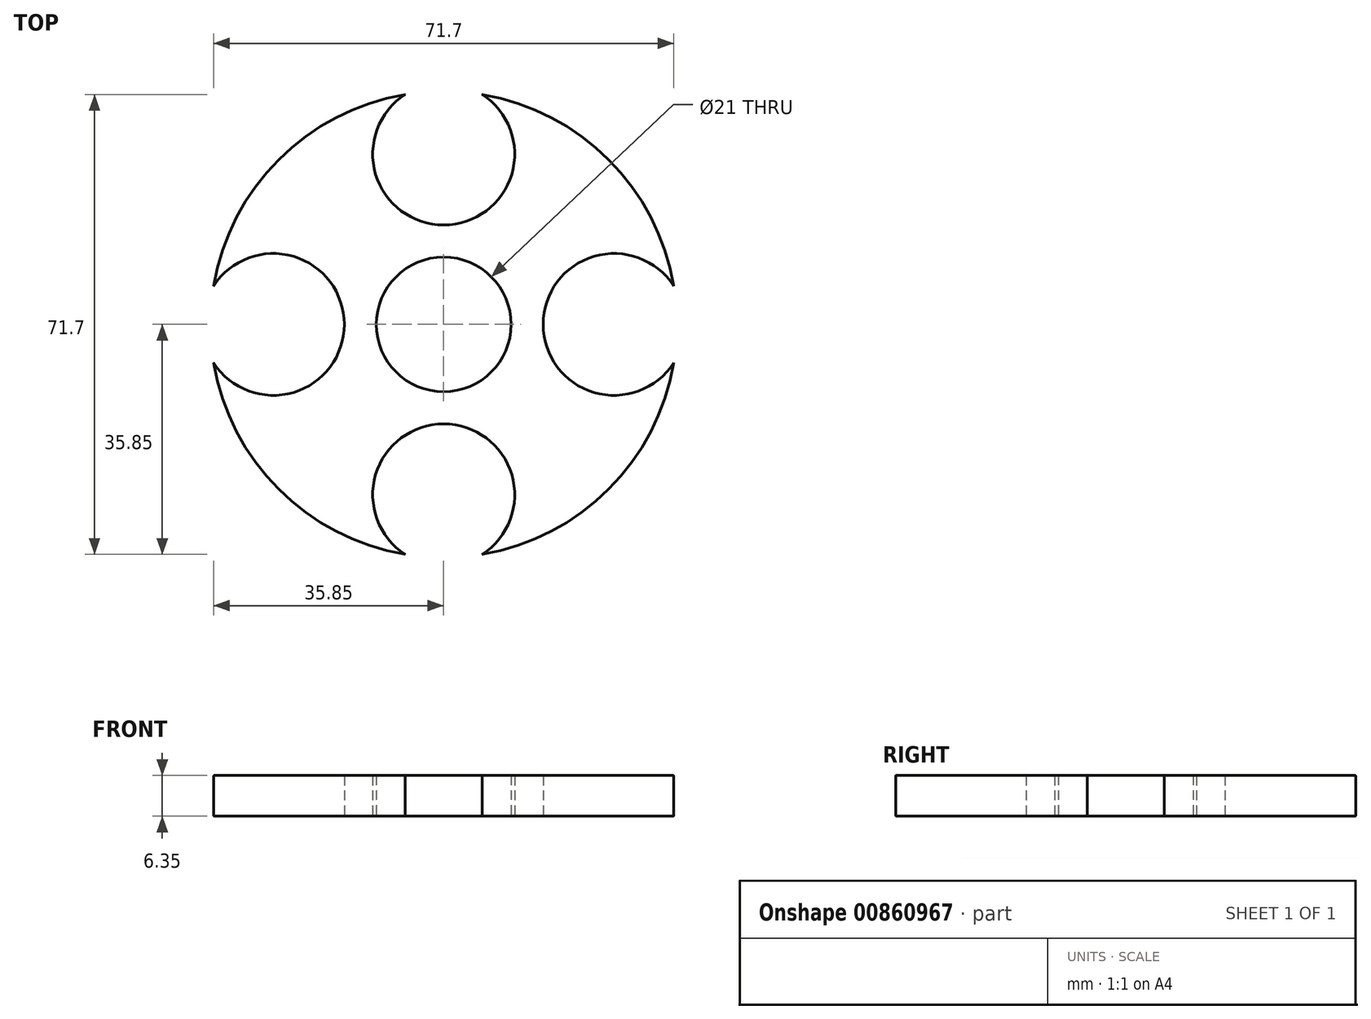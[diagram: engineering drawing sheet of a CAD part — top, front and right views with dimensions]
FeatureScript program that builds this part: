
annotation { "Feature Type Name" : "Feature", "Feature Type Description" : "" }
export const myFeature = defineFeature(function(context is Context, id is Id, definition is map)
    precondition{}
    {
        {
            var Q0;
            Q0=qCreatedBy(makeId("Top.planeOp"),FACE);
            var sketch = newSketch(context, id + "F0", { "sketchPlane" : qUnion([Q0])});
            skCircle(sketch, "E0", {"center": v(0, 0) * mm, "radius": 10.5 * mm});
            skArc(sketch, "E1", {"start": v(-35.85, -6) * mm, "mid": v(-25.7, -25.7) * mm, "end": v(-6.01, -35.85) * mm});
            skLineSegment(sketch, "E2", {"start": v(0, 10.5) * mm, "end": v(0, -11.46) * mm, "construction": true});
            skPoint(sketch, "E3.endSnap0", {"position": v(0, -0.48) * mm});
            skLineSegment(sketch, "E4", {"start": v(-10.5, 0) * mm, "end": v(10.5, 0) * mm, "construction": true});
            skArc(sketch, "E5.MirrorC", {"start": v(6.01, 35.85) * mm, "mid": v(0, 15.5) * mm, "end": v(-6.01, 35.85) * mm});
            skArc(sketch, "E6.MirrorC", {"start": v(6.01, -35.85) * mm, "mid": v(0, -15.5) * mm, "end": v(-6.01, -35.85) * mm});
            skArc(sketch, "E7", {"start": v(-35.85, -6) * mm, "mid": v(-15.5, 0) * mm, "end": v(-35.85, 6) * mm});
            skArc(sketch, "E8.MirrorC", {"start": v(35.85, -6) * mm, "mid": v(15.5, 0) * mm, "end": v(35.85, 6) * mm});
            skArc(sketch, "E9.trimOffspring", {"start": v(-6.01, 35.85) * mm, "mid": v(-25.7, 25.7) * mm, "end": v(-35.85, 6) * mm});
            skArc(sketch, "E10.trimOffspring", {"start": v(35.85, 6) * mm, "mid": v(25.7, 25.7) * mm, "end": v(6.01, 35.85) * mm});
            skArc(sketch, "E11.trimOffspring", {"start": v(6.01, -35.85) * mm, "mid": v(25.7, -25.7) * mm, "end": v(35.85, -6) * mm});
            skSolve(sketch);
        }
        {
            var Q0;
            Q0 = qSketchRegion(id + "F0", true);
            extrude(context, id + "F1", {"entities" : qUnion([Q0]), "depth" : 6.35 * mm, "offsetDistance" : 25.4 * mm});
        }
        {
            var Q0;
            Q0=makeQuery(id+"F1.opExtrude","CAP_EDGE",EDGE,{"disambiguationData":[OSD([sQuery(id+"F0.wireOp",EDGE,"E9.trimOffspring")])],"isStart":true});
            var Q1;
            Q1=makeQuery(id+"F1.opExtrude","CAP_EDGE",EDGE,{"disambiguationData":[OSD([sQuery(id+"F0.wireOp",EDGE,"E10.trimOffspring")])],"isStart":true});
            var Q2;
            Q2=makeQuery(id+"F1.opExtrude","CAP_EDGE",EDGE,{"disambiguationData":[OSD([sQuery(id+"F0.wireOp",EDGE,"E11.trimOffspring")])],"isStart":true});
            var Q3;
            Q3=makeQuery(id+"F1.opExtrude","CAP_EDGE",EDGE,{"disambiguationData":[OSD([sQuery(id+"F0.wireOp",EDGE,"E6.MirrorC")])],"isStart":true});
            var Q4;
            Q4=makeQuery(id+"F1.opExtrude","CAP_EDGE",EDGE,{"disambiguationData":[OSD([sQuery(id+"F0.wireOp",EDGE,"E8.MirrorC")])],"isStart":true});
            var Q5;
            Q5=makeQuery(id+"F1.opExtrude","CAP_EDGE",EDGE,{"disambiguationData":[OSD([sQuery(id+"F0.wireOp",EDGE,"E5.MirrorC")])],"isStart":true});
            var Q6;
            Q6=makeQuery(id+"F1.opExtrude","CAP_EDGE",EDGE,{"disambiguationData":[OSD([sQuery(id+"F0.wireOp",EDGE,"E7")])],"isStart":true});
            var Q7;
            Q7=makeQuery(id+"F1.opExtrude","CAP_EDGE",EDGE,{"disambiguationData":[OSD([sQuery(id+"F0.wireOp",EDGE,"E1")])],"isStart":true});
            var Q8;
            Q8=makeQuery(id+"F1.opExtrude","CAP_EDGE",EDGE,{"disambiguationData":[OSD([sQuery(id+"F0.wireOp",EDGE,"E1")])],"isStart":false});
            var Q9;
            Q9=makeQuery(id+"F1.opExtrude","CAP_EDGE",EDGE,{"disambiguationData":[OSD([sQuery(id+"F0.wireOp",EDGE,"E9.trimOffspring")])],"isStart":false});
            var Q10;
            Q10=makeQuery(id+"F1.opExtrude","CAP_EDGE",EDGE,{"disambiguationData":[OSD([sQuery(id+"F0.wireOp",EDGE,"E10.trimOffspring")])],"isStart":false});
            var Q11;
            Q11=makeQuery(id+"F1.opExtrude","CAP_EDGE",EDGE,{"disambiguationData":[OSD([sQuery(id+"F0.wireOp",EDGE,"E8.MirrorC")])],"isStart":false});
            var Q12;
            Q12=makeQuery(id+"F1.opExtrude","CAP_EDGE",EDGE,{"disambiguationData":[OSD([sQuery(id+"F0.wireOp",EDGE,"E5.MirrorC")])],"isStart":false});
            var Q13;
            Q13=makeQuery(id+"F1.opExtrude","CAP_EDGE",EDGE,{"disambiguationData":[OSD([sQuery(id+"F0.wireOp",EDGE,"E7")])],"isStart":false});
            var Q14;
            Q14=makeQuery(id+"F1.opExtrude","CAP_EDGE",EDGE,{"disambiguationData":[OSD([sQuery(id+"F0.wireOp",EDGE,"E6.MirrorC")])],"isStart":false});
            var Q15;
            Q15=makeQuery(id+"F1.opExtrude","CAP_EDGE",EDGE,{"disambiguationData":[OSD([sQuery(id+"F0.wireOp",EDGE,"E11.trimOffspring")])],"isStart":false});
            fillet(context, id + "F2", {"entities" : qUnion([Q0, Q1, Q2, Q3, Q4, Q5, Q6, Q7, Q8, Q9, Q10, Q11, Q12, Q13, Q14, Q15]), "radius" : 0.05 * mm, "tangentPropagation" : true, "allowEdgeOverflow" : false});
        }
    });
